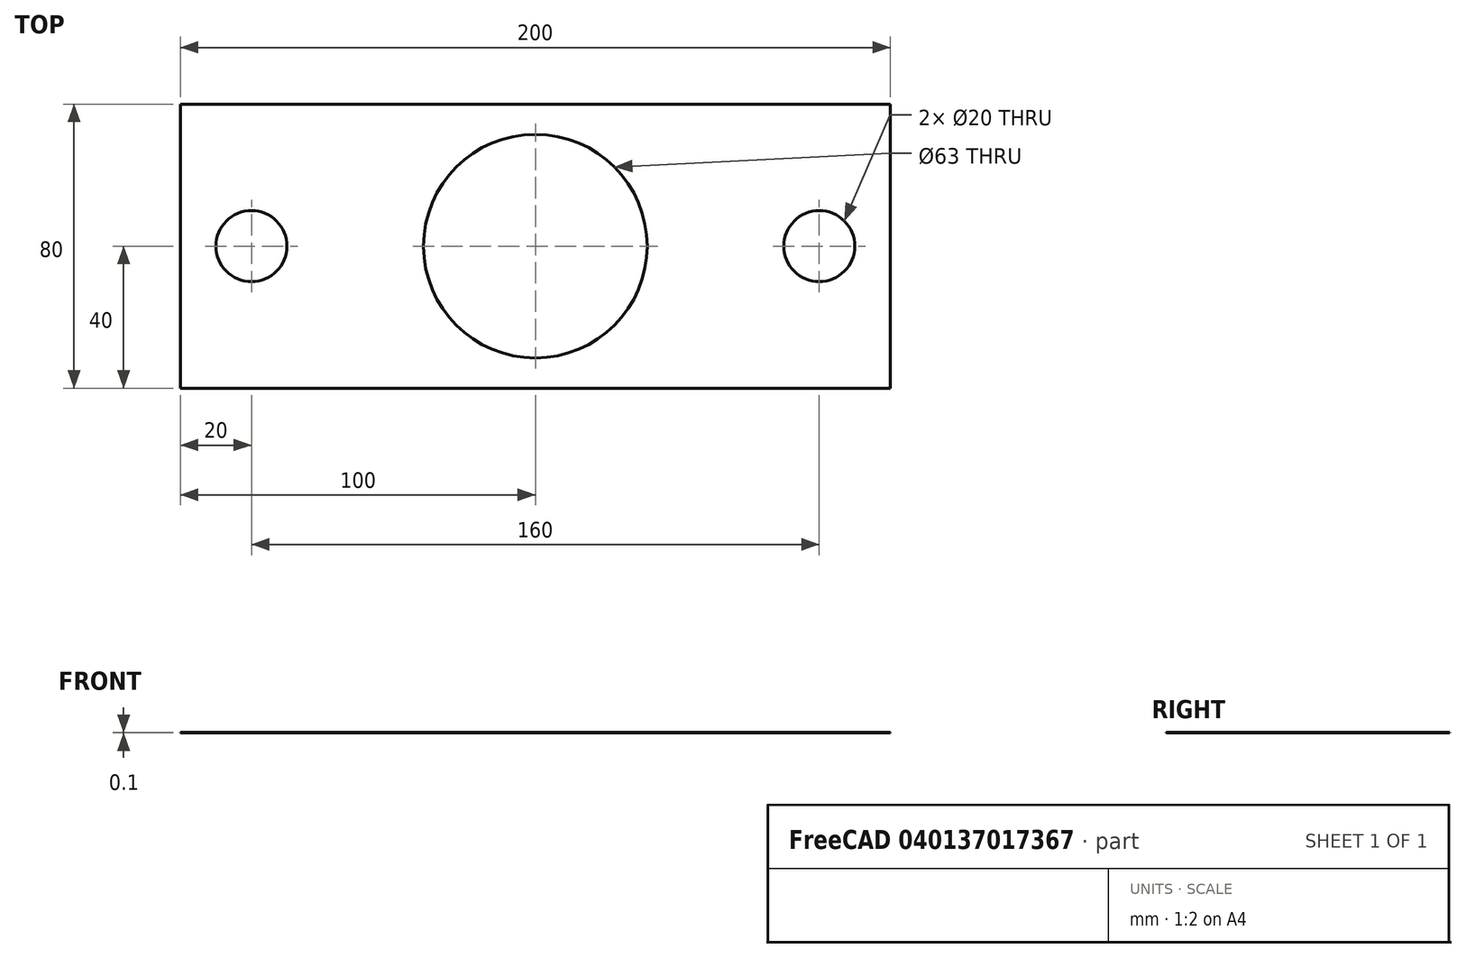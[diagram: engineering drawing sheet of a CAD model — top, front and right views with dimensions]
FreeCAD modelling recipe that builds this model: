
FCSTD DOCUMENT  (FreeCAD 0.19R24276 (Git))
Label: Master_sketch_P13
License: All rights reserved
LicenseURL: http://en.wikipedia.org/wiki/All_rights_reserved
objects: Sketcher::SketchObject×1, PartDesign::Pad×1, PartDesign::Body×1
note: 4 computed .brp shape members not serialized (recipe doc carries the construction recipe); baked Part::Feature solids carry a one-line shape summary decoded from their .brp

FEATURE [Sketcher::SketchObject] Sketch
  FullyConstrained = true
  MapMode = 5
  Support = -> [XY_Plane]
  sketch-geometry (7):
    g0: LineSegment StartX=-100 StartY=40 StartZ=0 EndX=100 EndY=40 EndZ=0
    g1: LineSegment StartX=100 StartY=40 StartZ=0 EndX=100 EndY=-40 EndZ=0
    g2: LineSegment StartX=100 StartY=-40 StartZ=0 EndX=-100 EndY=-40 EndZ=0
    g3: LineSegment StartX=-100 StartY=-40 StartZ=0 EndX=-100 EndY=40 EndZ=0
    g4: Circle CenterX=0 CenterY=0 CenterZ=0 NormalX=0 NormalY=0 NormalZ=1 AngleXU=0 Radius=31.5
    g5: Circle CenterX=80 CenterY=0 CenterZ=0 NormalX=0 NormalY=0 NormalZ=1 AngleXU=0 Radius=10
    g6: Circle CenterX=-80 CenterY=0 CenterZ=0 NormalX=0 NormalY=0 NormalZ=1 AngleXU=0 Radius=10
  constraints (19):
    c: Coincident(g0,g1)
    c: Coincident(g1,g2)
    c: Coincident(g2,g3)
    c: Coincident(g3,g0)
    c: Horizontal(g0)
    c: Horizontal(g2)
    c: Vertical(g1)
    c: Vertical(g3)
    c: Symmetric(g0,g1,g-1)
    c: DistanceY(g1,g1) = 80
    c: DistanceX(g2,g2) = 200
    c: Coincident(g4,g-1)
    c: Diameter(g4) = 63
    c: PointOnObject(g5,g-1)
    c: PointOnObject(g6,g-1)
    c: DistanceX(g4,g5) = 80
    c: DistanceX(g6,g4) = 80
    c: Diameter(g5) = 20
    c: Diameter(g6) = 20
FEATURE [PartDesign::Pad] Pad
  Direction = (1,1,1)
  Length = 0.1
  Length2 = 100
  Profile = -> Sketch
  Type = 0
FEATURE [PartDesign::Body] Body
  Group = -> [Sketch,Pad]
  Origin = -> Origin
  Tip = -> Pad
